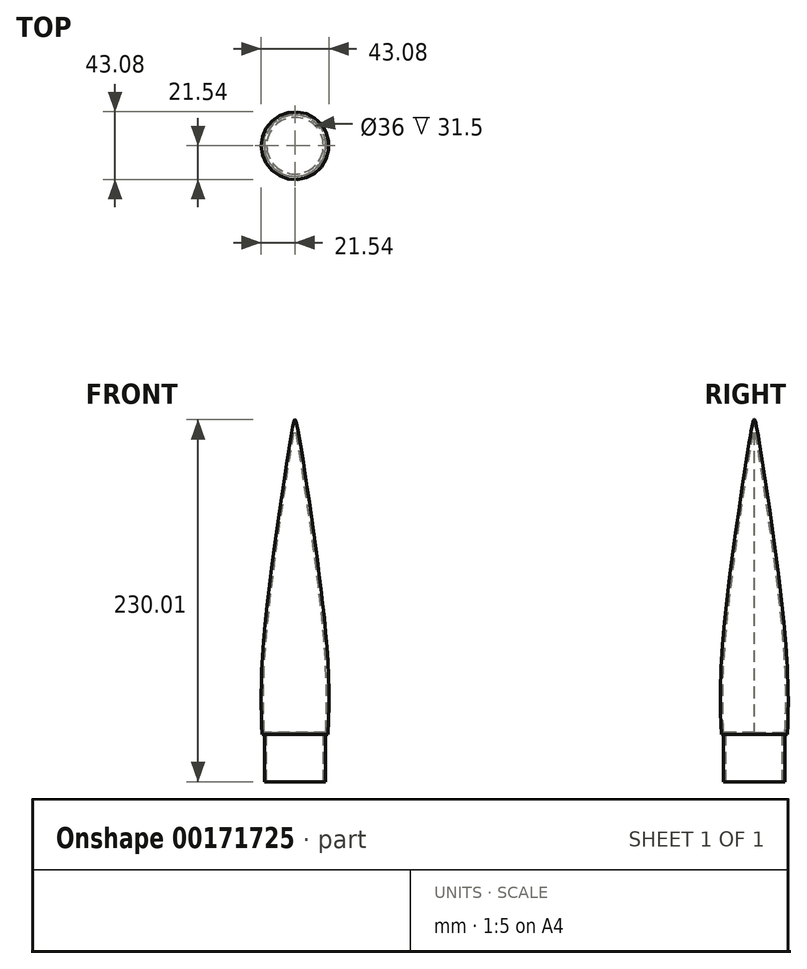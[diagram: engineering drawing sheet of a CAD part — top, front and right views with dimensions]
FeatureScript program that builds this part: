
annotation { "Feature Type Name" : "Feature", "Feature Type Description" : "" }
export const myFeature = defineFeature(function(context is Context, id is Id, definition is map)
    precondition{}
    {
        {
            var Q0;
            Q0=qCreatedBy(makeId("Front.planeOp"),FACE);
            var sketch = newSketch(context, id + "F0", { "sketchPlane" : qUnion([Q0])});
            skLineSegment(sketch, "E0", {"start": v(21, 0) * mm, "end": v(-21, 0) * mm, "construction": true});
            skLineSegment(sketch, "E1", {"start": v(0, 0) * mm, "end": v(0, 200) * mm, "construction": true});
            skLineSegment(sketch, "E2", {"start": v(-21, 0) * mm, "end": v(-21, 382.94) * mm, "construction": true});
            skFitSpline(sketch, "E3", {"points": [v(-21, 0) * mm, v(-18.95, 70.3) * mm, v(-0.63, 199.48) * mm, v(-0.37, 199.9) * mm, v(-0.15, 200) * mm, v(0, 200) * mm], "startDerivative": vector(-5.07, 137.53) * mm, "endDerivative": vector(7.74, -1) * mm});
            skLineSegment(sketch, "E4", {"start": v(0, 200) * mm, "end": v(0, -30) * mm});
            skLineSegment(sketch, "E5", {"start": v(-21, 0) * mm, "end": v(-19.5, 0) * mm});
            skLineSegment(sketch, "E6", {"start": v(-19.5, 0) * mm, "end": v(-19.5, -30) * mm});
            skLineSegment(sketch, "E7", {"start": v(0, -30) * mm, "end": v(-19.5, -30) * mm});
            skSolve(sketch);
        }
        {
            var Q0;
            Q0=makeQuery(id+"F0.imprint","IMPRINT",FACE,{"disambiguationData":[TD([[makeQuery(id+"F0.imprint","IMPRINT",EDGE,{"derivedFrom":sQuery(id+"F0.wireOp",EDGE,"E3")}),-1.0]])]});
            var Q1;
            Q1=sQuery(id+"F0.wireOp",EDGE,"E4");
            revolve(context, id + "F1", {"entities" : qUnion([Q0]), "axis" : qUnion([Q1]), "revolveType" : RevolveType.FULL});
        }
        {
            var Q0;
            Q0=makeQuery(id+"F1.opRevolve","SWEPT_FACE",FACE,{"disambiguationData":[OSD([sQuery(id+"F0.wireOp",EDGE,"E7")])]});
            shell(context, id + "F2", {"entities" : qUnion([Q0]), "thickness" : 1.5 * mm});
        }
    });
